# Revit family: VE_Heat Exchanger_F_MEPcontent_Vaillant_recoVAIR_VAR 60-2 D-DW_UA-UK
name_source: partatom
category: Mechanical Equipment
units: mm (PartAtom-declared; Revit-internal decimal feet)

## family parameters
Cut with Voids When Loaded = Yes
Host = Face
OmniClass Number = 23.75.10.34.21
OmniClass Title = Heat Exchangers for Ventilation Air
Part Type = Normal
Room Calculation Point = No
Round Connector Dimension = Use Diameter
Shared = No

## types (2) — shared parameters
Article Description = децентралізованим приладом, сумісний знаступними виробами: VAZ CP/2 Або VAZ RC/2
Back Panel Width = 212 mm  [stored 0.695538 ft]
Base Family Version = 23.06
Black = Color RGB 045-045-045
Bottom Clearance = 2000 mm  [stored 6.56168 ft]
Content Supplier URL = www.MEPcontent.com
Custom = No
Default Elevation = 2150 mm
Depth = 596 mm
Description = децентралізованим приладом, сумісний знаступними виробами: VAZ CP/2 Або VAZ RC/2
EMCS Version = 5.0
ETIM Article Class = EC011286
Family Version = 23.06
GLN = 4024074000007
Grey = Color RGB 111-106-099
Height = 250 mm  [stored 0.82021 ft]
Hole Diameter = 162 mm  [stored 0.531496 ft]
IFCExportAs = IfcHeatExchanger
IFCExportType = NOTDEFINED
Left Clearance = 100 mm  [stored 0.328084 ft]
MEPcontent Class = HEAT_EXCHANGER_VE
Manufacturer = Vaillant
Manufacturer URL = https://www.vaillant.ua
Maximum Flow = 40.0 m³/h
Phase = 1
Pipe Diameter = 160 mm  [stored 0.524934 ft]
Power = 0 W
Primary Volume Flow = 0.0 L/s
Product Line = recoVAIR
Revit Version = 2021
Right Clearance = 100 mm  [stored 0.328084 ft]
Secondary Volume Flow = 0.0 L/s
Sound power level, indoor (ErP) = 39
Top Clearance = 100 mm  [stored 0.328084 ft]
URL = https://mep.trimble.com
Voltage = 230 V
Weight = 3.50 kg
White = Color RGB 219-227-229
Width = 233 mm  [stored 0.764436 ft]

## per-type parameters (varying)
| type | GTIN | Manufacturer Art. No. |
| VAR 60-2 D | 4024074932728 | 0010047340 |
| VAR 60-2 DW | 4024074932742 | 0010047341 |

note: column(s) folded — value = type name in every type: Article Type, Model

note: [stored X ft] marks values corroborated as IEEE doubles in the binary element streams (Revit-internal decimal feet)

## geometry (parser evidence)
native form markers: Sweep x9
no freeform markers — native parametric forms only
